# Revit family: QF_ELECTROLUXPROFESSIONAL_1LSN7S_WB6-20_S
name_source: partatom
category: Attrezzature speciali
units: mm (PartAtom-declared; Revit-internal decimal feet)

## family parameters
Basato su piano di lavoro = No
Condiviso = No
Punto di calcolo locali = No
Quota connettore circolare = Usa diametro
Sempre verticale = Sì
Taglio con vuoti quando caricato = No
Tipo di parte = Normale

## types (10) — shared parameters
Cold Water Maximum Pressure = 0.00 psi
Cold Water Minimum Pressure = 0.00 psi
Cold Water Size = 1"
Conn Conduit = Sì
Depth Actual = 1050 mm
Electrical Remarks = 400 V/3N ph/50/60 Hz
Height Actual = 1640 mm  [stored 5.38058 ft]
Hot Water Consumption = 0 GPM
Hot Water Maximum Pressure = 0.00 psi
Hot Water Minimum Pressure = 0.00 psi
Hot Water Size = 1"
Hot Water Temperature = -460 °F
Indirect Waste Size = 1"
Latent Heat Output = 0.0
Length Actual = 915 mm  [stored 3.00197 ft]
Max Overcurrent Protection = 0 A
Min Ckt Ampacity = 0 A
Modello = WB6-20
Phase = 3
Produttore = Electrolux Professional
Sensible Heat Output = 0.0
Steam Pounds per Hour = 72
URL = www.electroluxprofessional.com
Weight = 670
Weight in Pounds = 55.1
zero-valued in all types: Cold Water Connection Height, Gas KW, Hot Water Connection Height, Indirect Waste Connection Height, Prospetto di default

## per-type parameters (varying)
| type | Descrizione | Volts | Watts |
| 9890030029 | WASHER WB6-20 200L 2DOORS RIGHT/RIGHT LOW STEAM 380-415/50/60/3 COMPASS PRO 2xWATER 13xLIQ. SILVER | 415 V | 6000 W |
| 9890030105 | WASHER WB6-20 200L 2DOORS RIGHT/LEFT DUAL STEAM+EL 380-415/50/60/3 COMPASS PRO 2xWATER 13xLIQ.+POWDER SILVER ALARM EXP. | 415 V | 15000 W |
| 9890030090 | WASHER WB6-20 200L 2DOORS LEFT/RIGHT DUAL STEAM+EL 230/50/60/3 2xCOMPASS PRO 3xWATER 13xLIQ.+POWDER 2xDRAIN SST AIDO IWS | 230 V | 15000 W |
| 9890030092 | WASHER WB6-20 200L 2DOORS RIGHT/RIGHT STEAM 380-415/50/60/3 2xCOMPASS PRO 2xWATER 13xLIQ.+POWDER SST AIDO ALARM EXP. | 415 V | 6000 W |
| 9890030111 | WASHER WB6-20 200L 2DOORS RIGHT/RIGHT STEAM 380-415/50/60/3 COMPASS PRO 2xWATER 13xLIQ.+POWDER SILVER EXP. | 415 V | 6000 W |
| 9890030067 | WASHER WB6-20 200L 2DOORS RIGHT/LEFT STEAM 380-415/50/60/3 COMPASS PRO 2xWATER 13xLIQ.+POWDER SILVER ALARM | 415 V | 6000 W |
| 9890030041 | WASHER WB6-20 200L 2DOORS RIGHT/RIGHT INDIRECT STEAM 380-415/50/60/3 2xCOMPASS PRO 3xWATER 13xLIQ. 2xDRAIN SST ALARM EXP | 415 V | 6000 W |
| 9890030034 | WASHER WB6-20 200L 2DOORS RIGHT/RIGHT STEAM 380-415/50/60/3 COMPASS PRO 2xWATER 13xLIQ.+POWDER SILVER EXP. | 415 V | 6000 W |
| 9890030066 | WASHER WB6-20 200L 2DOORS RIGHT/LEFT INDIRECT STEAM 380-415/50/60/3 2xCOMPASS PRO 3xWATER 13xLIQ.+POWDER SST ALARM BMP E | 415 V | 6000 W |
| 9893030004 | WASHER WB6-20 200L 2DOORS RIGHT/RIGHT STEAM 208-240/50/60/3 COMPASS PRO 2xWATER 13xLIQ.+POWDER SILVER ALARM EXP. ETL | 240 V | 6000 W |

note: [stored X ft] marks values corroborated as IEEE doubles in the binary element streams (Revit-internal decimal feet)

## geometry (parser evidence)
native form markers: Blend x8, Sweep x1
no freeform markers — native parametric forms only
